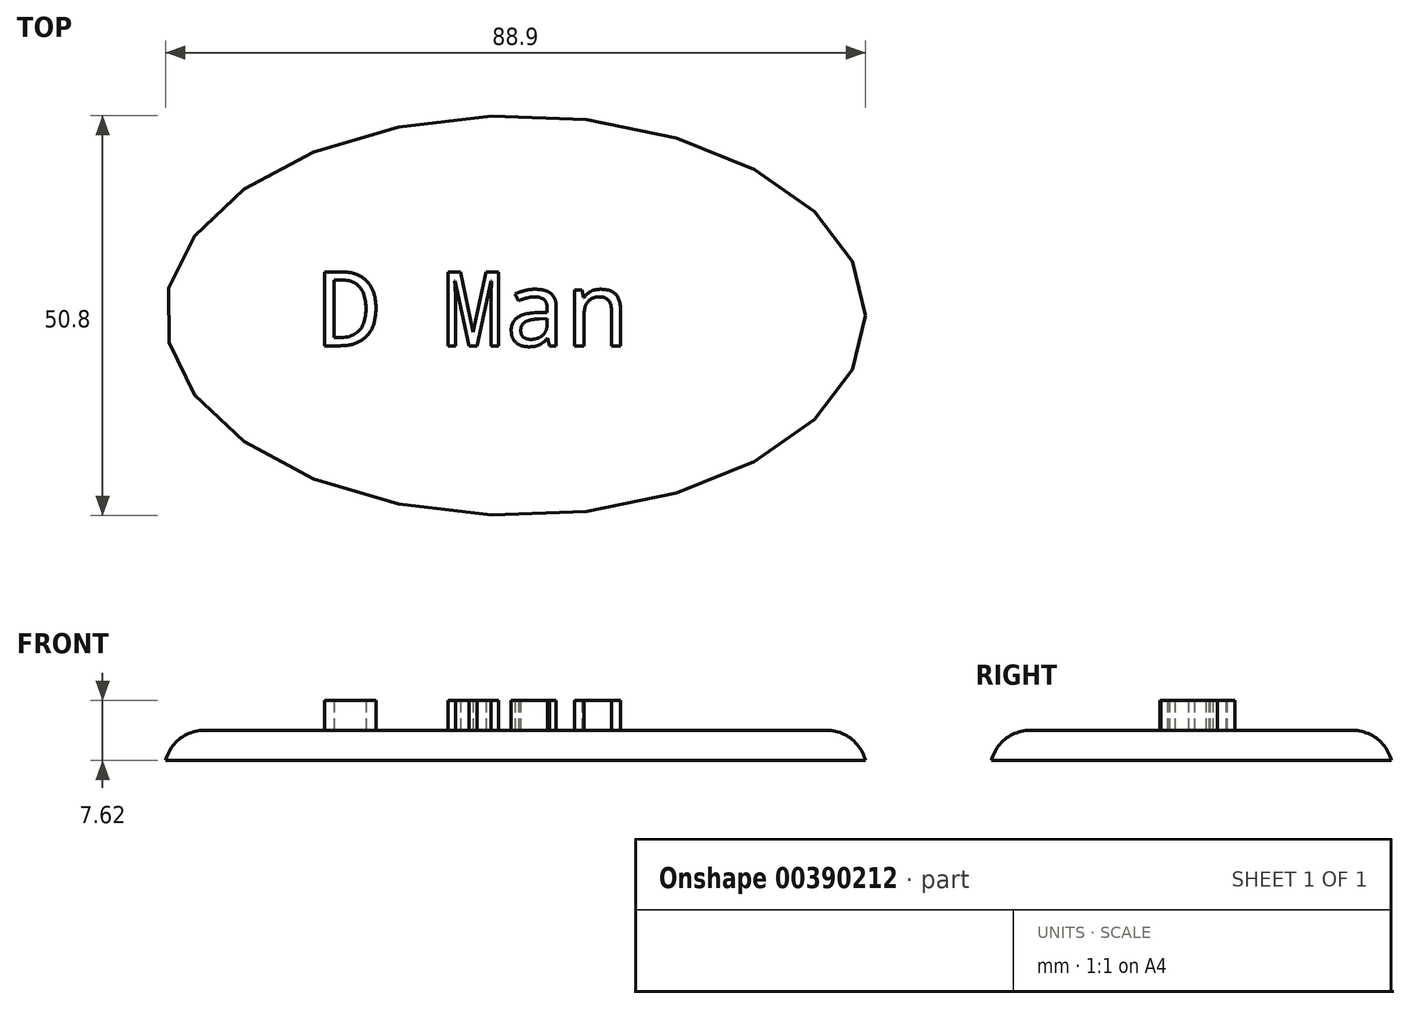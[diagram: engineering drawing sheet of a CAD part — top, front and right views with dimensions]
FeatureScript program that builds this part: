
annotation { "Feature Type Name" : "Feature", "Feature Type Description" : "" }
export const myFeature = defineFeature(function(context is Context, id is Id, definition is map)
    precondition{}
    {
        {
            var Q0;
            Q0=qCreatedBy(makeId("Top.planeOp"),FACE);
            var sketch = newSketch(context, id + "F0", { "sketchPlane" : qUnion([Q0])});
            skEllipse(sketch, "E0", {"center": v(-33.42, 6.36) * mm, "majorRadius": 44.45 * mm, "minorRadius": 25.4 * mm, "majorAxis": v(1, 0)});
            skSolve(sketch);
        }
        {
            var Q0;
            Q0=makeQuery(id+"F0.imprint","IMPRINT",FACE,{"disambiguationData":[TD([[makeQuery(id+"F0.imprint","IMPRINT",EDGE,{"derivedFrom":sQuery(id+"F0.wireOp",EDGE,"E0")}),1.0]])]});
            extrude(context, id + "F1", {"entities" : qUnion([Q0]), "depth" : 3.8 * mm});
        }
        {
            var Q0;
            Q0=qCreatedBy(makeId("Top.planeOp"),FACE);
            var sketch = newSketch(context, id + "F2", { "sketchPlane" : qUnion([Q0])});
            skText(sketch, "E1", { "text": "D Man", "fontName": "OpenSans-Regular.ttf"});
            const initialGuessF2  = {"E1": [-0.06, 0, 1, 0, 0.01198]};
            skSetInitialGuess(sketch, initialGuessF2);
            skSolve(sketch);
        }
        {
            var Q0;
            Q0 = qSketchRegion(id + "F2", true);
            extrude(context, id + "F3", {"entities" : qUnion([Q0]), "operationType" : NewBodyOperationType.REMOVE, "oppositeDirection" : true, "depth" : 2.54 * mm});
        }
        {
            var Q0;
            Q0=makeQuery(id+"F1.opExtrude","CAP_FACE",FACE,{"disambiguationData":[OSD([sQuery(id+"F0.wireOp",EDGE,"E0")])],"isStart":false});
            var sketch = newSketch(context, id + "F4", { "sketchPlane" : qUnion([Q0])});
            skText(sketch, "E2", { "text": "D Man", "fontName": "DroidSansMono.ttf"});
            const initialGuessF4  = {"E2": [-0.05852, 0.00251, 1, 0, 0.00947]};
            skSetInitialGuess(sketch, initialGuessF4);
            skSolve(sketch);
        }
        {
            var Q0;
            Q0 = qSketchRegion(id + "F4", true);
            extrude(context, id + "F5", {"entities" : qUnion([Q0]), "operationType" : NewBodyOperationType.ADD, "depth" : 3.8 * mm});
        }
        {
            var Q0;
            Q0=makeQuery(id+"F1.opExtrude","CAP_EDGE",EDGE,{"disambiguationData":[OSD([sQuery(id+"F0.wireOp",EDGE,"E0")])],"isStart":false});
            fillet(context, id + "F6", {"entities" : qUnion([Q0]), "radius" : 5.08 * mm, "tangentPropagation" : true, "allowEdgeOverflow" : false});
        }
    });
